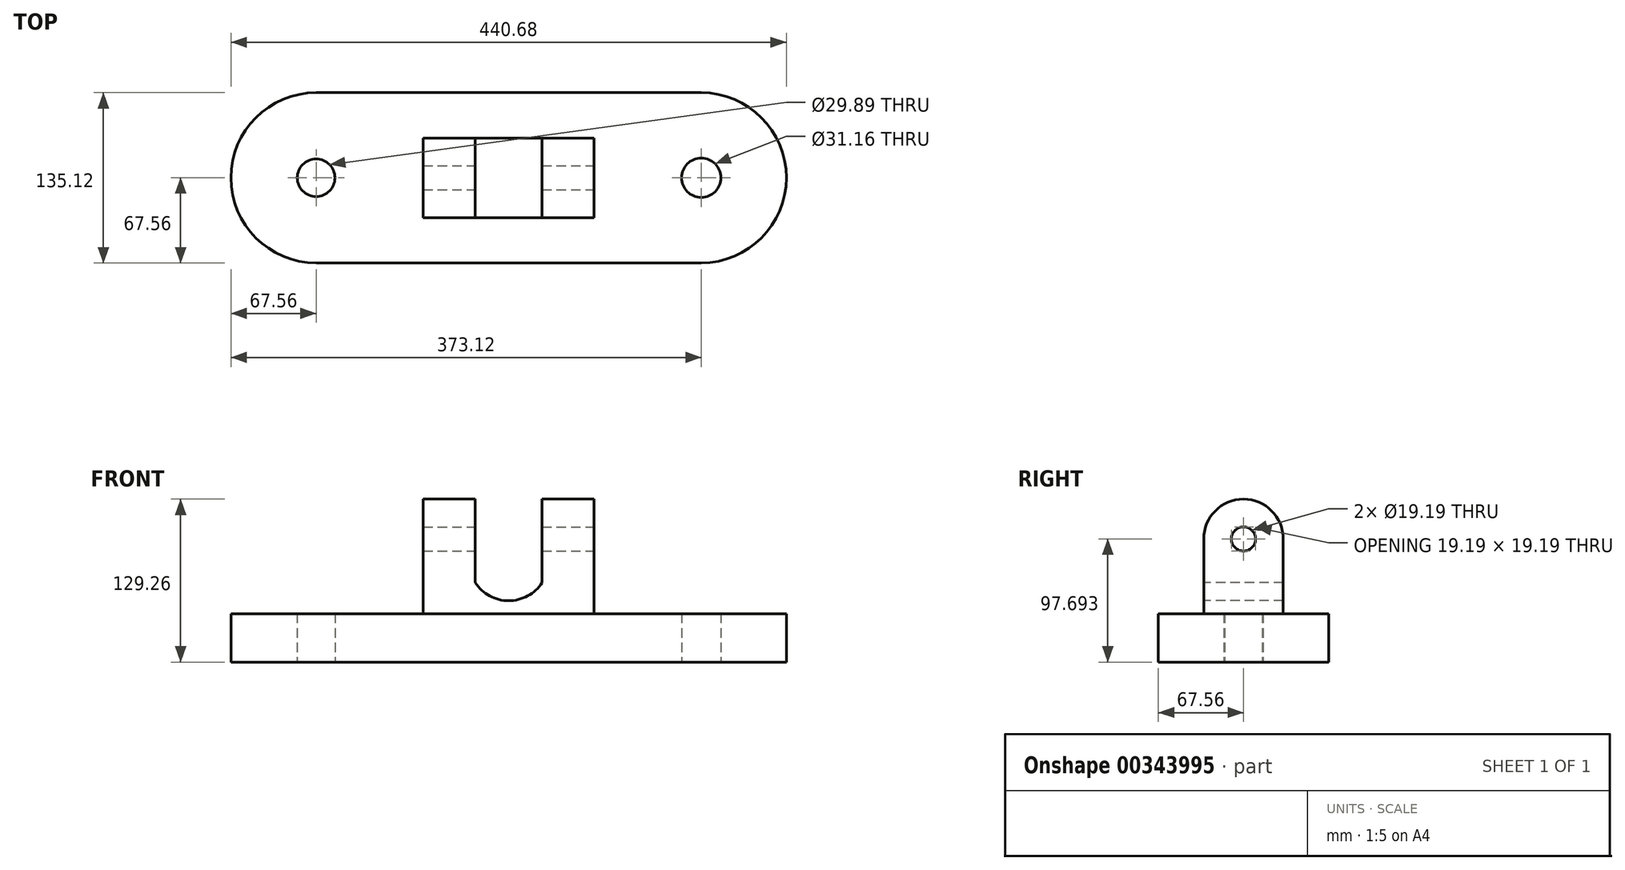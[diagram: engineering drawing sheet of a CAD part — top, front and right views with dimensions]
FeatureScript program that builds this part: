
annotation { "Feature Type Name" : "Feature", "Feature Type Description" : "" }
export const myFeature = defineFeature(function(context is Context, id is Id, definition is map)
    precondition{}
    {
        {
            var Q0;
            Q0=qCreatedBy(makeId("Top.planeOp"),FACE);
            var sketch = newSketch(context, id + "F0", { "sketchPlane" : qUnion([Q0])});
            skLineSegment(sketch, "E0.bottom", {"start": v(152.78, 67.56) * mm, "end": v(-152.78, 67.56) * mm});
            skLineSegment(sketch, "E0.top", {"start": v(152.78, -67.56) * mm, "end": v(-152.78, -67.56) * mm});
            skPoint(sketch, "E0.middle", {"position": v(0, 0) * mm});
            skArc(sketch, "E1", {"start": v(152.78, -67.56) * mm, "mid": v(220.34, 0) * mm, "end": v(152.78, 67.56) * mm});
            skArc(sketch, "E2", {"start": v(-152.78, 67.56) * mm, "mid": v(-220.34, 0) * mm, "end": v(-152.78, -67.56) * mm});
            skCircle(sketch, "E3", {"center": v(-152.78, 0) * mm, "radius": 14.95 * mm});
            skCircle(sketch, "E4", {"center": v(152.78, 0) * mm, "radius": 15.58 * mm});
            skSolve(sketch);
        }
        {
            var Q0;
            Q0=makeQuery(id+"F0.imprint","IMPRINT",FACE,{"disambiguationData":[TD([[makeQuery(id+"F0.imprint","IMPRINT",EDGE,{"derivedFrom":sQuery(id+"F0.wireOp",EDGE,"E0.bottom")}),1.0]])]});
            extrude(context, id + "F1", {"entities" : qUnion([Q0]), "depth" : 38.35 * mm});
        }
        {
            var Q0;
            Q0=qCreatedBy(makeId("Right.planeOp"),FACE);
            var sketch = newSketch(context, id + "F2", { "sketchPlane" : qUnion([Q0])});
            skLineSegment(sketch, "E5.left", {"start": v(-31.57, 97.7) * mm, "end": v(-31.57, 38.35) * mm});
            skLineSegment(sketch, "E5.right", {"start": v(31.57, 97.7) * mm, "end": v(31.57, 38.35) * mm});
            skPoint(sketch, "E5.middle", {"position": v(0, 39.34) * mm});
            skLineSegment(sketch, "E6.0", {"start": v(-31.57, 38.35) * mm, "end": v(31.57, 38.35) * mm});
            skPoint(sketch, "E7.orphan", {"position": v(67.56, 38.35) * mm});
            skPoint(sketch, "E8.orphan", {"position": v(-67.56, 38.35) * mm});
            skPoint(sketch, "E5.top.start.orphan", {"position": v(-31.57, -19.01) * mm});
            skPoint(sketch, "E9.orphan", {"position": v(31.57, -19.01) * mm});
            skArc(sketch, "E10", {"start": v(31.57, 97.7) * mm, "mid": v(0, 129.26) * mm, "end": v(-31.57, 97.7) * mm});
            skCircle(sketch, "E11", {"center": v(0, 97.7) * mm, "radius": 9.6 * mm});
            skSolve(sketch);
        }
        {
            var Q0;
            Q0=makeQuery(id+"F2.imprint","IMPRINT",FACE,{"disambiguationData":[TD([[makeQuery(id+"F2.imprint","IMPRINT",EDGE,{"derivedFrom":sQuery(id+"F2.wireOp",EDGE,"E5.left")}),1.0]])]});
            extrude(context, id + "F3", {"entities" : qUnion([Q0]), "operationType" : NewBodyOperationType.ADD, "endBound" : BoundingType.SYMMETRIC, "oppositeDirection" : true, "depth" : 135.64 * mm});
        }
        {
            var Q0;
            Q0=qCreatedBy(makeId("Front.planeOp"),FACE);
            var sketch = newSketch(context, id + "F4", { "sketchPlane" : qUnion([Q0])});
            skLineSegment(sketch, "E12.bottom", {"start": v(26.5, 133.1) * mm, "end": v(-26.5, 133.1) * mm});
            skLineSegment(sketch, "E12.left", {"start": v(26.5, 133.1) * mm, "end": v(26.5, 63.08) * mm});
            skLineSegment(sketch, "E12.right", {"start": v(-26.5, 133.1) * mm, "end": v(-26.5, 63.08) * mm});
            skPoint(sketch, "E12.middle", {"position": v(0, 98.1) * mm});
            skArc(sketch, "E13", {"start": v(-26.5, 63.08) * mm, "mid": v(0, 48.63) * mm, "end": v(26.5, 63.08) * mm});
            skSolve(sketch);
        }
        {
            var Q0;
            Q0=makeQuery(id+"F4.imprint","IMPRINT",FACE,{"disambiguationData":[TD([[makeQuery(id+"F4.imprint","IMPRINT",EDGE,{"derivedFrom":sQuery(id+"F4.wireOp",EDGE,"E12.bottom")}),1.0]])]});
            extrude(context, id + "F5", {"entities" : qUnion([Q0]), "operationType" : NewBodyOperationType.REMOVE, "endBound" : BoundingType.SYMMETRIC, "oppositeDirection" : true, "depth" : 117.86 * mm});
        }
    });
